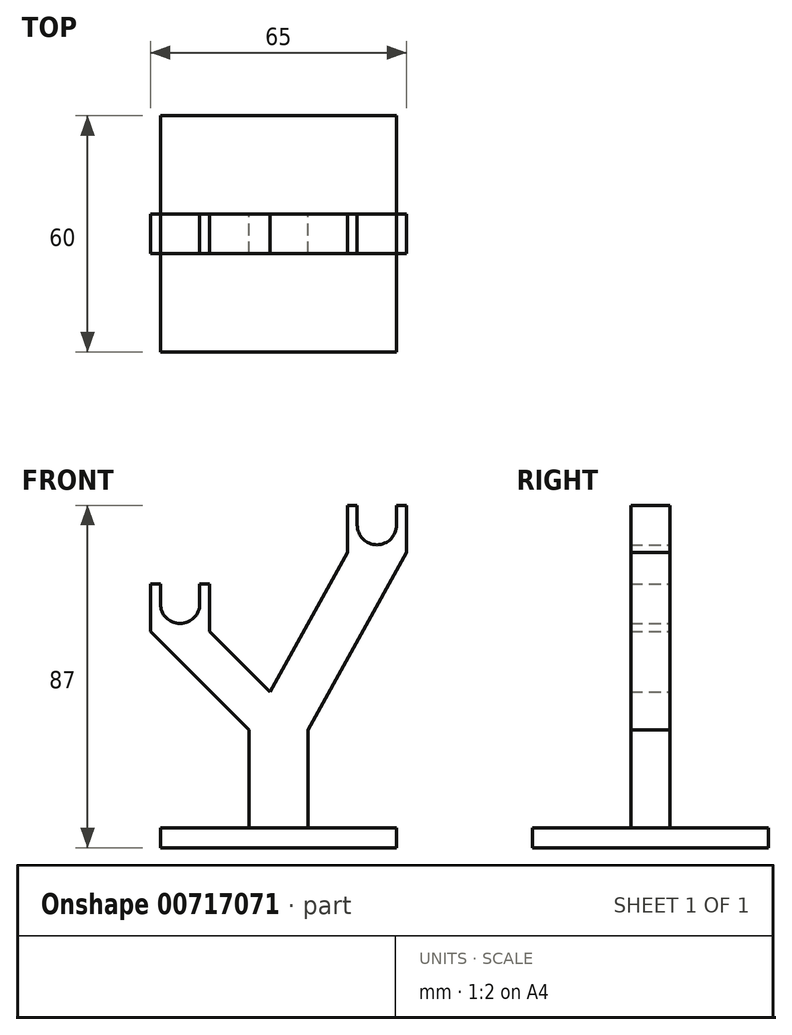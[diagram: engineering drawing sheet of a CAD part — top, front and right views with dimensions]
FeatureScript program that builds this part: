
annotation { "Feature Type Name" : "Feature", "Feature Type Description" : "" }
export const myFeature = defineFeature(function(context is Context, id is Id, definition is map)
    precondition{}
    {
        {
            var Q0;
            Q0=qCreatedBy(makeId("Front.planeOp"),FACE);
            var sketch = newSketch(context, id + "F0", { "sketchPlane" : qUnion([Q0])});
            skArc(sketch, "E0", {"start": v(-5, 0) * mm, "mid": v(0, -5) * mm, "end": v(5, 0) * mm});
            skLineSegment(sketch, "E1", {"start": v(-5, 0) * mm, "end": v(5, 0) * mm});
            skLineSegment(sketch, "E2", {"start": v(5, 0) * mm, "end": v(5, -7) * mm});
            skLineSegment(sketch, "E3", {"start": v(5, -7) * mm, "end": v(-5, -7) * mm});
            skLineSegment(sketch, "E4", {"start": v(-5, -7) * mm, "end": v(-5, 0) * mm});
            skArc(sketch, "E5", {"start": v(45, 20) * mm, "mid": v(50, 15) * mm, "end": v(55, 20) * mm});
            skLineSegment(sketch, "E6", {"start": v(45, 20) * mm, "end": v(55, 20) * mm});
            skLineSegment(sketch, "E7", {"start": v(55, 20) * mm, "end": v(55, 13) * mm});
            skLineSegment(sketch, "E8", {"start": v(55, 13) * mm, "end": v(45, 13) * mm});
            skLineSegment(sketch, "E9", {"start": v(45, 13) * mm, "end": v(45, 20) * mm});
            skLineSegment(sketch, "E10", {"start": v(-5, -57) * mm, "end": v(55, -57) * mm});
            skLineSegment(sketch, "E11", {"start": v(-5, -57) * mm, "end": v(-5, -62) * mm});
            skLineSegment(sketch, "E12", {"start": v(-5, -62) * mm, "end": v(55, -62) * mm});
            skLineSegment(sketch, "E13", {"start": v(55, -62) * mm, "end": v(55, -57) * mm});
            skLineSegment(sketch, "E14", {"start": v(17.5, -57) * mm, "end": v(17.5, -32) * mm});
            skLineSegment(sketch, "E15", {"start": v(17.5, -32) * mm, "end": v(32.5, -32) * mm});
            skLineSegment(sketch, "E16", {"start": v(32.5, -32) * mm, "end": v(32.5, -57) * mm});
            skLineSegment(sketch, "E17", {"start": v(-5, 0) * mm, "end": v(-7.5, 0) * mm});
            skLineSegment(sketch, "E18", {"start": v(-7.5, 0) * mm, "end": v(-7.5, -7) * mm});
            skLineSegment(sketch, "E19", {"start": v(-7.5, -7) * mm, "end": v(-5, -7) * mm});
            skLineSegment(sketch, "E20", {"start": v(5, 0) * mm, "end": v(7.5, 0) * mm});
            skLineSegment(sketch, "E21", {"start": v(7.5, 0) * mm, "end": v(7.5, -7) * mm});
            skLineSegment(sketch, "E22", {"start": v(7.5, -7) * mm, "end": v(5, -7) * mm});
            skLineSegment(sketch, "E23", {"start": v(45, 20) * mm, "end": v(42.5, 20) * mm});
            skLineSegment(sketch, "E24", {"start": v(42.5, 20) * mm, "end": v(42.5, 13) * mm});
            skLineSegment(sketch, "E25", {"start": v(42.5, 13) * mm, "end": v(45, 13) * mm});
            skLineSegment(sketch, "E26", {"start": v(55, 20) * mm, "end": v(57.5, 20) * mm});
            skLineSegment(sketch, "E27", {"start": v(57.5, 20) * mm, "end": v(57.5, 13) * mm});
            skLineSegment(sketch, "E28", {"start": v(57.5, 13) * mm, "end": v(55, 13) * mm});
            skLineSegment(sketch, "E29", {"start": v(17.5, -32) * mm, "end": v(-7.5, -7) * mm});
            skLineSegment(sketch, "E30", {"start": v(32.5, -32) * mm, "end": v(7.5, -7) * mm});
            skLineSegment(sketch, "E31", {"start": v(32.5, -32) * mm, "end": v(57.5, 13) * mm});
            skLineSegment(sketch, "E32", {"start": v(17.5, -32) * mm, "end": v(42.5, 13) * mm});
            skLineSegment(sketch, "E33", {"start": v(55, 20) * mm, "end": v(55, 25) * mm});
            skLineSegment(sketch, "E34", {"start": v(55, 25) * mm, "end": v(57.5, 25) * mm});
            skLineSegment(sketch, "E35", {"start": v(57.5, 25) * mm, "end": v(57.5, 20) * mm});
            skLineSegment(sketch, "E36", {"start": v(42.5, 20) * mm, "end": v(42.5, 25) * mm});
            skLineSegment(sketch, "E37", {"start": v(42.5, 25) * mm, "end": v(45, 25) * mm});
            skLineSegment(sketch, "E38", {"start": v(45, 25) * mm, "end": v(45, 20) * mm});
            skLineSegment(sketch, "E39", {"start": v(7.5, 0) * mm, "end": v(7.5, 5) * mm});
            skLineSegment(sketch, "E40", {"start": v(7.5, 5) * mm, "end": v(5, 5) * mm});
            skLineSegment(sketch, "E41", {"start": v(5, 5) * mm, "end": v(5, 0) * mm});
            skLineSegment(sketch, "E42", {"start": v(-5, 0) * mm, "end": v(-5, 5) * mm});
            skLineSegment(sketch, "E43", {"start": v(-5, 5) * mm, "end": v(-7.5, 5) * mm});
            skLineSegment(sketch, "E44", {"start": v(-7.5, 5) * mm, "end": v(-7.5, 0) * mm});
            skSolve(sketch);
        }
        {
            var Q0;
            {var subQ0=sQuery(id+"F0.wireOp",EDGE,"E11");Q0=makeQuery(id+"F0.imprint","IMPRINT",FACE,{"disambiguationData":[TD([[makeQuery(id+"F0.imprint","IMPRINT",EDGE,{"derivedFrom":subQ0}),1.0]])]});}
            extrude(context, id + "F1", {"entities" : qUnion([Q0]), "depth" : 30 * mm, "offsetDistance" : 25 * mm, "hasSecondDirection" : true, "secondDirectionOppositeDirection" : true, "secondDirectionDepth" : 30 * mm});
        }
        {
            var Q0;
            {var subQ0=sQuery(id+"F0.wireOp",EDGE,"E14");Q0=makeQuery(id+"F0.imprint","IMPRINT",FACE,{"disambiguationData":[TD([[makeQuery(id+"F0.imprint","IMPRINT",EDGE,{"derivedFrom":subQ0}),-1.0]])]});}
            var Q1;
            {var subQ0=sQuery(id+"F0.wireOp",EDGE,"E15");Q1=makeQuery(id+"F0.imprint","IMPRINT",FACE,{"disambiguationData":[TD([[makeQuery(id+"F0.imprint","IMPRINT",EDGE,{"derivedFrom":subQ0}),1.0]])]});}
            var Q2;
            Q2=makeQuery(id+"F0.imprint","IMPRINT",FACE,{"disambiguationData":[TD([[makeQuery(id+"F0.imprint","IMPRINT",EDGE,{"derivedFrom":sQuery(id+"F0.wireOp",EDGE,"E8")}),1.0]])]});
            var Q3;
            Q3=makeQuery(id+"F0.imprint","IMPRINT",FACE,{"disambiguationData":[TD([[makeQuery(id+"F0.imprint","IMPRINT",EDGE,{"derivedFrom":sQuery(id+"F0.wireOp",EDGE,"E3")}),1.0]])]});
            var Q4;
            Q4=makeQuery(id+"F0.imprint","IMPRINT",FACE,{"disambiguationData":[TD([[makeQuery(id+"F0.imprint","IMPRINT",EDGE,{"derivedFrom":sQuery(id+"F0.wireOp",EDGE,"E7")}),1.0]])]});
            var Q5;
            Q5=makeQuery(id+"F0.imprint","IMPRINT",FACE,{"disambiguationData":[TD([[makeQuery(id+"F0.imprint","IMPRINT",EDGE,{"derivedFrom":sQuery(id+"F0.wireOp",EDGE,"E5")}),-1.0]])]});
            var Q6;
            Q6=makeQuery(id+"F0.imprint","IMPRINT",FACE,{"disambiguationData":[TD([[makeQuery(id+"F0.imprint","IMPRINT",EDGE,{"derivedFrom":sQuery(id+"F0.wireOp",EDGE,"E9")}),1.0]])]});
            var Q7;
            Q7=makeQuery(id+"F0.imprint","IMPRINT",FACE,{"disambiguationData":[TD([[makeQuery(id+"F0.imprint","IMPRINT",EDGE,{"derivedFrom":sQuery(id+"F0.wireOp",EDGE,"E2")}),1.0]])]});
            var Q8;
            Q8=makeQuery(id+"F0.imprint","IMPRINT",FACE,{"disambiguationData":[TD([[makeQuery(id+"F0.imprint","IMPRINT",EDGE,{"derivedFrom":sQuery(id+"F0.wireOp",EDGE,"E0")}),-1.0]])]});
            var Q9;
            Q9=makeQuery(id+"F0.imprint","IMPRINT",FACE,{"disambiguationData":[TD([[makeQuery(id+"F0.imprint","IMPRINT",EDGE,{"derivedFrom":sQuery(id+"F0.wireOp",EDGE,"E4")}),1.0]])]});
            var Q10;
            Q10=makeQuery(id+"F0.imprint","IMPRINT",FACE,{"disambiguationData":[TD([[makeQuery(id+"F0.imprint","IMPRINT",EDGE,{"derivedFrom":sQuery(id+"F0.wireOp",EDGE,"E23")}),-1.0]])]});
            var Q11;
            Q11=makeQuery(id+"F0.imprint","IMPRINT",FACE,{"disambiguationData":[TD([[makeQuery(id+"F0.imprint","IMPRINT",EDGE,{"derivedFrom":sQuery(id+"F0.wireOp",EDGE,"E26")}),1.0]])]});
            var Q12;
            Q12=makeQuery(id+"F0.imprint","IMPRINT",FACE,{"disambiguationData":[TD([[makeQuery(id+"F0.imprint","IMPRINT",EDGE,{"derivedFrom":sQuery(id+"F0.wireOp",EDGE,"E20")}),1.0]])]});
            var Q13;
            Q13=makeQuery(id+"F0.imprint","IMPRINT",FACE,{"disambiguationData":[TD([[makeQuery(id+"F0.imprint","IMPRINT",EDGE,{"derivedFrom":sQuery(id+"F0.wireOp",EDGE,"E17")}),-1.0]])]});
            extrude(context, id + "F2", {"entities" : qUnion([Q0, Q1, Q2, Q3, Q4, Q5, Q6, Q7, Q8, Q9, Q10, Q11, Q12, Q13]), "operationType" : NewBodyOperationType.ADD, "depth" : 5 * mm, "offsetDistance" : 25 * mm, "hasSecondDirection" : true, "secondDirectionOppositeDirection" : true, "secondDirectionDepth" : 5 * mm});
        }
    });
